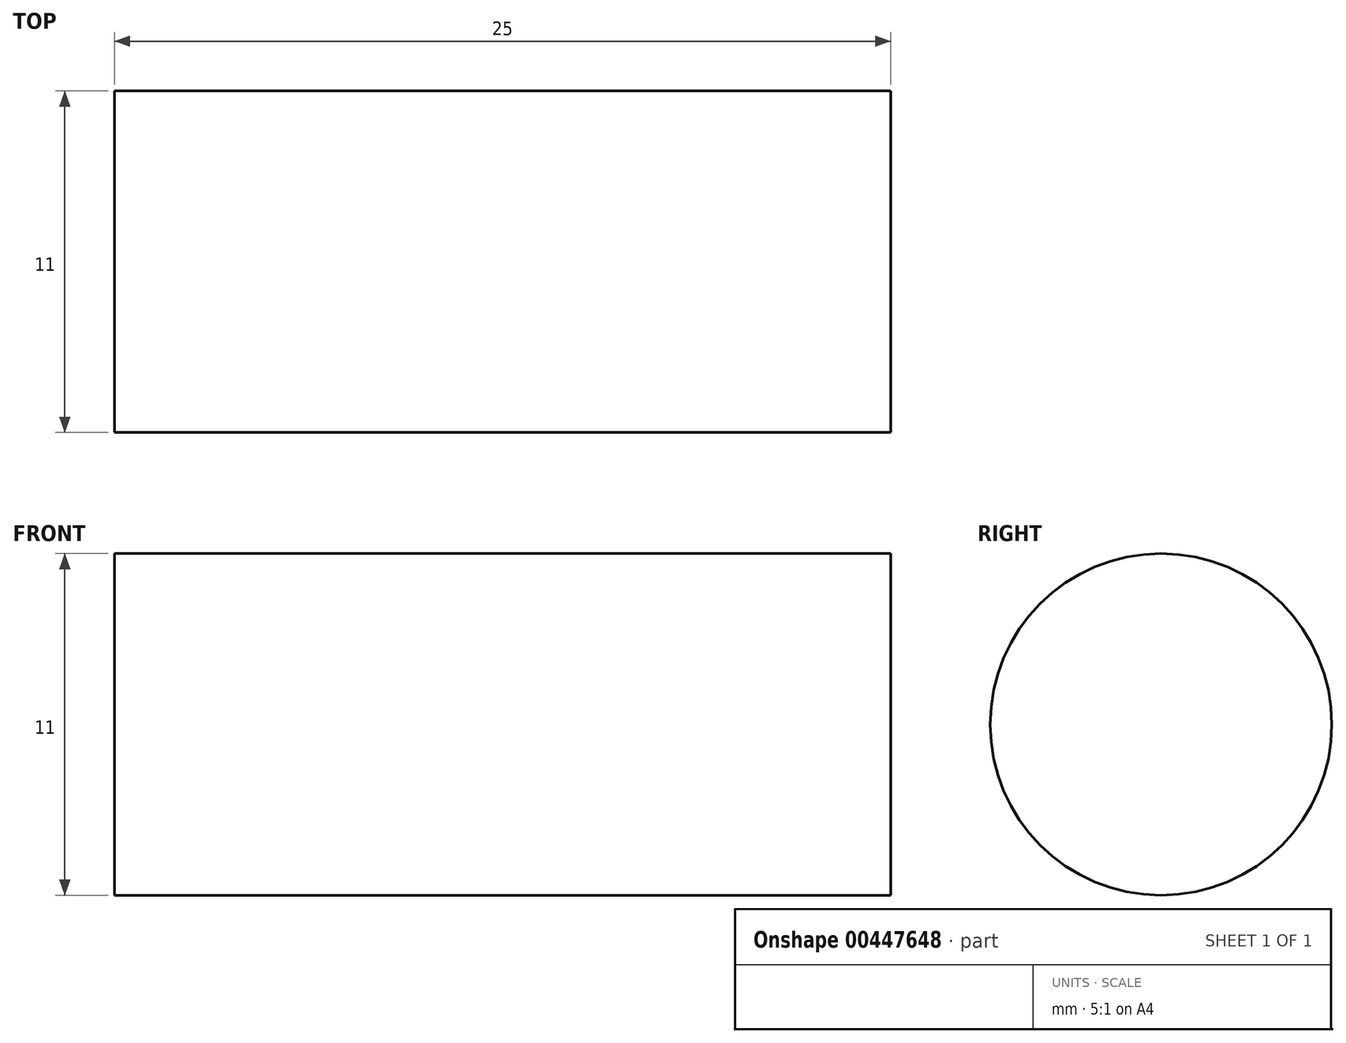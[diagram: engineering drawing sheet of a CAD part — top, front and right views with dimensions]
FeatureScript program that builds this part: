
annotation { "Feature Type Name" : "Feature", "Feature Type Description" : "" }
export const myFeature = defineFeature(function(context is Context, id is Id, definition is map)
    precondition{}
    {
        {
            var Q0;
            Q0=qCreatedBy(makeId("Right.planeOp"),FACE);
            var sketch = newSketch(context, id + "F0", { "sketchPlane" : qUnion([Q0])});
            skCircle(sketch, "E0", {"center": v(0, 0) * mm, "radius": 5.5 * mm});
            skSolve(sketch);
        }
        {
            var Q0;
            Q0 = qSketchRegion(id + "F0", true);
            extrude(context, id + "F1", {"entities" : qUnion([Q0]), "depth" : 25 * mm});
        }
    });
